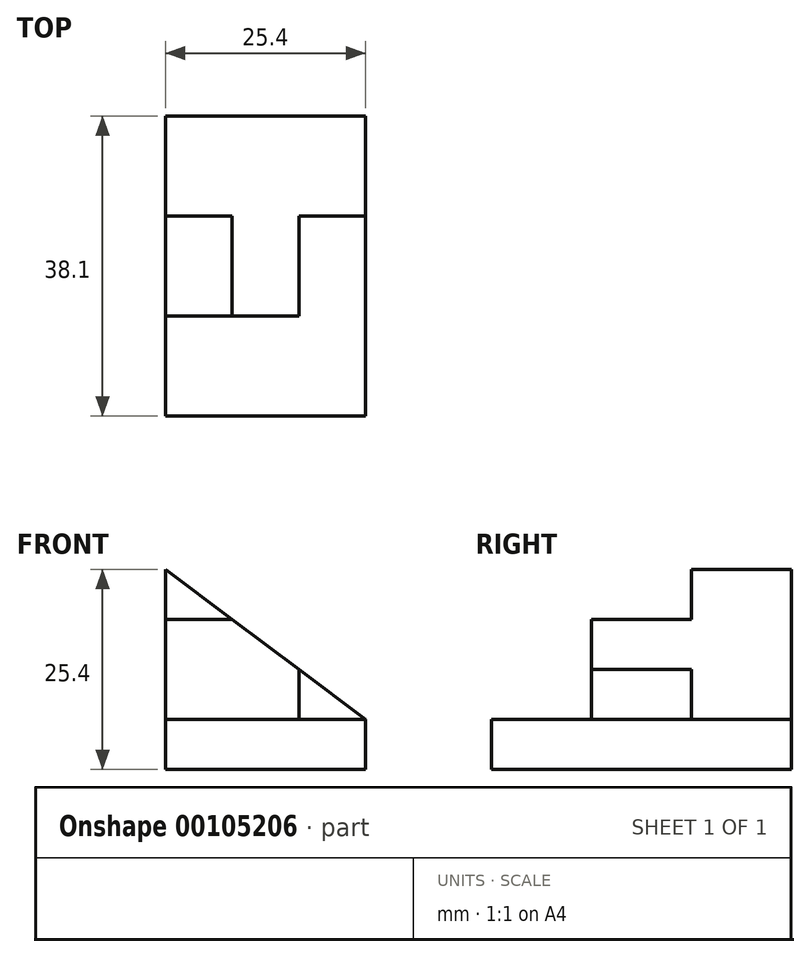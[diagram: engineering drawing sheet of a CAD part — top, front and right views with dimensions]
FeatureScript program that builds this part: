
annotation { "Feature Type Name" : "Feature", "Feature Type Description" : "" }
export const myFeature = defineFeature(function(context is Context, id is Id, definition is map)
    precondition{}
    {
        {
            var Q0;
            Q0=qCreatedBy(makeId("Front.planeOp"),FACE);
            var sketch = newSketch(context, id + "F0", { "sketchPlane" : qUnion([Q0])});
            skLineSegment(sketch, "E0", {"start": v(0, 0) * mm, "end": v(25.4, 0) * mm});
            skLineSegment(sketch, "E1", {"start": v(25.4, 0) * mm, "end": v(25.4, 6.35) * mm});
            skLineSegment(sketch, "E2", {"start": v(25.4, 6.35) * mm, "end": v(0, 6.35) * mm});
            skLineSegment(sketch, "E3", {"start": v(0, 6.35) * mm, "end": v(0, 0) * mm});
            skSolve(sketch);
        }
        {
            var Q0;
            Q0 = qSketchRegion(id + "F0", true);
            extrude(context, id + "F1", {"entities" : qUnion([Q0]), "depth" : 38.1 * mm});
        }
        {
            var Q0;
            Q0=qCreatedBy(makeId("Front.planeOp"),FACE);
            var sketch = newSketch(context, id + "F2", { "sketchPlane" : qUnion([Q0])});
            skLineSegment(sketch, "E4", {"start": v(0, 6.35) * mm, "end": v(0, 25.4) * mm});
            skLineSegment(sketch, "E5", {"start": v(0, 25.4) * mm, "end": v(25.4, 6.35) * mm});
            skLineSegment(sketch, "E6", {"start": v(25.4, 6.35) * mm, "end": v(0, 6.35) * mm});
            skSolve(sketch);
        }
        {
            var Q0;
            Q0=makeQuery(id+"F2.imprint","IMPRINT",FACE,{"disambiguationData":[TD([[makeQuery(id+"F2.imprint","IMPRINT",EDGE,{"derivedFrom":sQuery(id+"F2.wireOp",EDGE,"E4")}),-1.0]])]});
            extrude(context, id + "F3", {"entities" : qUnion([Q0]), "operationType" : NewBodyOperationType.ADD, "depth" : 12.7 * mm});
        }
        {
            var Q0;
            Q0=qCreatedBy(makeId("Front.planeOp"),FACE);
            var sketch = newSketch(context, id + "F4", { "sketchPlane" : qUnion([Q0])});
            skLineSegment(sketch, "E7", {"start": v(0, 6.35) * mm, "end": v(0, 19.05) * mm});
            skLineSegment(sketch, "E8", {"start": v(0, 19.05) * mm, "end": v(8.47, 19.05) * mm});
            skLineSegment(sketch, "E9", {"start": v(8.47, 19.05) * mm, "end": v(16.93, 12.7) * mm});
            skLineSegment(sketch, "E10", {"start": v(16.93, 12.7) * mm, "end": v(16.93, 6.35) * mm});
            skLineSegment(sketch, "E11", {"start": v(16.93, 6.35) * mm, "end": v(0, 6.35) * mm});
            skSolve(sketch);
        }
        {
            var Q0;
            Q0=makeQuery(id+"F4.imprint","IMPRINT",FACE,{"disambiguationData":[TD([[makeQuery(id+"F4.imprint","IMPRINT",EDGE,{"derivedFrom":sQuery(id+"F4.wireOp",EDGE,"E7")}),-1.0]])]});
            extrude(context, id + "F5", {"entities" : qUnion([Q0]), "operationType" : NewBodyOperationType.ADD, "depth" : 25.4 * mm});
        }
    });
